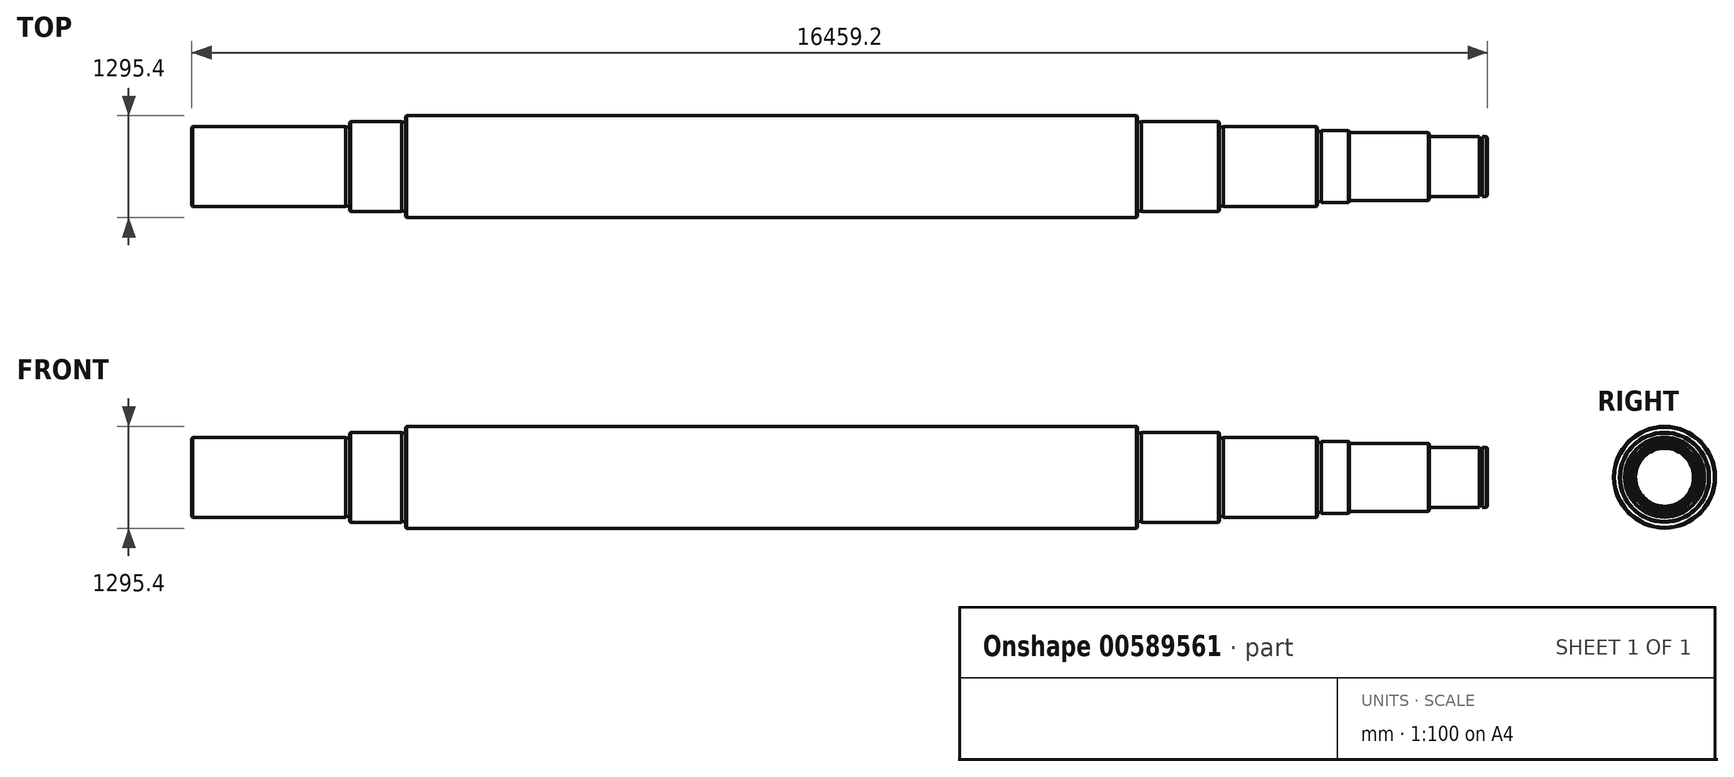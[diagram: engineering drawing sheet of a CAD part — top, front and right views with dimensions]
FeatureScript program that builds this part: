
annotation { "Feature Type Name" : "Feature", "Feature Type Description" : "" }
export const myFeature = defineFeature(function(context is Context, id is Id, definition is map)
    precondition{}
    {
        {
            var Q0;
            Q0=qCreatedBy(makeId("Front.planeOp"),FACE);
            var sketch = newSketch(context, id + "F0", { "sketchPlane" : qUnion([Q0])});
            skLineSegment(sketch, "E0", {"start": v(-2750.42, 3212.24) * mm, "end": v(-2750.42, 3174.14) * mm});
            skLineSegment(sketch, "E1", {"start": v(-2750.42, 3212.24) * mm, "end": v(-2763.12, 3224.94) * mm});
            skLineSegment(sketch, "E2", {"start": v(-4122.02, 3237.64) * mm, "end": v(-4122.02, 3250.34) * mm});
            skLineSegment(sketch, "E3", {"start": v(-5366.62, 3293.52) * mm, "end": v(-5366.62, 3301.14) * mm});
            skLineSegment(sketch, "E4", {"start": v(-3766.42, 3224.94) * mm, "end": v(-2763.12, 3224.94) * mm});
            skLineSegment(sketch, "E5", {"start": v(-4122.02, 3250.34) * mm, "end": v(-3779.12, 3250.34) * mm});
            skLineSegment(sketch, "E6", {"start": v(-5366.62, 3301.14) * mm, "end": v(-4185.52, 3301.14) * mm});
            skLineSegment(sketch, "E7", {"start": v(-4172.82, 3237.64) * mm, "end": v(-4122.02, 3237.64) * mm});
            skLineSegment(sketch, "E8", {"start": v(-5417.42, 3293.52) * mm, "end": v(-5366.62, 3293.52) * mm});
            skLineSegment(sketch, "E9", {"start": v(-2082.4, 3174.14) * mm, "end": v(-2026.52, 3174.14) * mm});
            skLineSegment(sketch, "E10", {"start": v(-6408.02, 3364.64) * mm, "end": v(-5430.12, 3364.64) * mm});
            skLineSegment(sketch, "E11", {"start": v(-15742.52, 3440.84) * mm, "end": v(-6471.52, 3440.84) * mm});
            skLineSegment(sketch, "E12", {"start": v(-16453.72, 3364.64) * mm, "end": v(-15806.02, 3364.64) * mm});
            skLineSegment(sketch, "E13", {"start": v(-18460.32, 3301.14) * mm, "end": v(-16517.22, 3301.14) * mm});
            skLineSegment(sketch, "E14", {"start": v(-16517.22, 3293.52) * mm, "end": v(-16466.42, 3293.52) * mm});
            skLineSegment(sketch, "E15", {"start": v(-15806.02, 3357.02) * mm, "end": v(-15755.22, 3357.02) * mm});
            skLineSegment(sketch, "E16", {"start": v(-6458.82, 3357.02) * mm, "end": v(-6408.02, 3357.02) * mm});
            skLineSegment(sketch, "E17", {"start": v(-2115.42, 3156.36) * mm, "end": v(-2082.4, 3156.36) * mm});
            skLineSegment(sketch, "E18", {"start": v(-4172.82, 3288.44) * mm, "end": v(-4172.82, 3237.64) * mm});
            skLineSegment(sketch, "E19", {"start": v(-3766.42, 3237.64) * mm, "end": v(-3766.42, 3224.94) * mm});
            skLineSegment(sketch, "E20", {"start": v(-2013.82, 3161.44) * mm, "end": v(-2013.82, 2793.14) * mm});
            skLineSegment(sketch, "E21", {"start": v(-5417.42, 3351.94) * mm, "end": v(-5417.42, 3293.52) * mm});
            skLineSegment(sketch, "E22", {"start": v(-6458.82, 3428.14) * mm, "end": v(-6458.82, 3357.02) * mm});
            skLineSegment(sketch, "E23", {"start": v(-18473.02, 2793.14) * mm, "end": v(-18473.02, 3288.44) * mm});
            skLineSegment(sketch, "E24", {"start": v(-4172.82, 3288.44) * mm, "end": v(-4185.52, 3301.14) * mm});
            skLineSegment(sketch, "E25", {"start": v(-3766.42, 3237.64) * mm, "end": v(-3779.12, 3250.34) * mm});
            skLineSegment(sketch, "E26", {"start": v(-2013.82, 3161.44) * mm, "end": v(-2026.52, 3174.14) * mm});
            skLineSegment(sketch, "E27", {"start": v(-5417.42, 3351.94) * mm, "end": v(-5430.12, 3364.64) * mm});
            skLineSegment(sketch, "E28", {"start": v(-6458.82, 3428.14) * mm, "end": v(-6471.52, 3440.84) * mm});
            skLineSegment(sketch, "E29", {"start": v(-15755.22, 3428.14) * mm, "end": v(-15742.52, 3440.84) * mm});
            skLineSegment(sketch, "E30", {"start": v(-16466.42, 3351.94) * mm, "end": v(-16453.72, 3364.64) * mm});
            skLineSegment(sketch, "E31", {"start": v(-18473.02, 3288.44) * mm, "end": v(-18460.32, 3301.14) * mm});
            skLineSegment(sketch, "E32", {"start": v(-3779.12, 3250.34) * mm, "end": v(-4024.76, 3250.34) * mm});
            skLineSegment(sketch, "E33", {"start": v(-2750.42, 3174.14) * mm, "end": v(-2115.42, 3174.14) * mm});
            skLineSegment(sketch, "E34", {"start": v(-2115.42, 3156.36) * mm, "end": v(-2115.42, 3174.14) * mm});
            skLineSegment(sketch, "E35", {"start": v(-2082.4, 3156.36) * mm, "end": v(-2082.4, 3174.14) * mm});
            skLineSegment(sketch, "E36.trimOffspring", {"start": v(-6408.02, 3357.02) * mm, "end": v(-6408.02, 3364.64) * mm});
            skLineSegment(sketch, "E37.trimOffspring", {"start": v(-15806.02, 3364.64) * mm, "end": v(-15920.33, 3364.64) * mm});
            skLineSegment(sketch, "E38.trimOffspring", {"start": v(-15755.22, 3357.02) * mm, "end": v(-15755.22, 3428.14) * mm});
            skLineSegment(sketch, "E39.trimOffspring", {"start": v(-15806.02, 3357.02) * mm, "end": v(-15806.02, 3364.64) * mm});
            skLineSegment(sketch, "E40.trimOffspring", {"start": v(-16466.42, 3293.52) * mm, "end": v(-16466.42, 3351.94) * mm});
            skLineSegment(sketch, "E41.trimOffspring", {"start": v(-16517.22, 3293.52) * mm, "end": v(-16517.22, 3301.14) * mm});
            skLineSegment(sketch, "E42", {"start": v(-20310.56, 2793.14) * mm, "end": v(-1104.15, 2793.14) * mm, "construction": true});
            skLineSegment(sketch, "E43", {"start": v(-18473.02, 2793.14) * mm, "end": v(-2013.82, 2793.14) * mm});
            skSolve(sketch);
        }
        {
            var Q0;
            Q0=makeQuery(id+"F0.imprint","IMPRINT",FACE,{"disambiguationData":[TD([[makeQuery(id+"F0.imprint","IMPRINT",EDGE,{"derivedFrom":sQuery(id+"F0.wireOp",EDGE,"E0")}),-1.0]])]});
            var Q1;
            Q1=sQuery(id+"F0.wireOp",EDGE,"E42");
            revolve(context, id + "F1", {"entities" : qUnion([Q0]), "axis" : qUnion([Q1]), "revolveType" : RevolveType.FULL});
        }
    });
